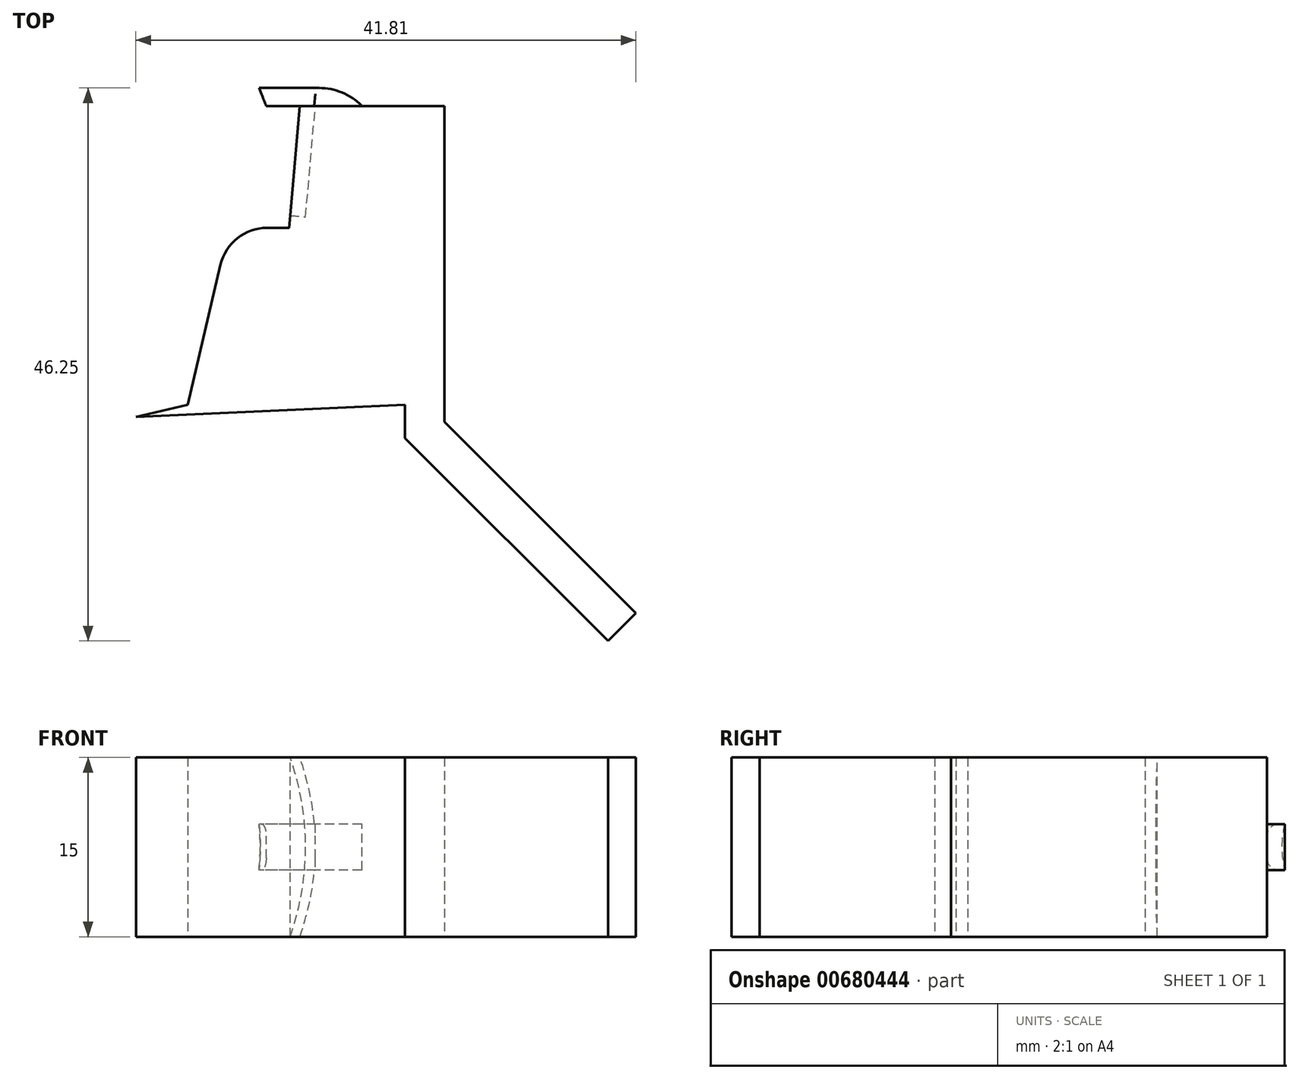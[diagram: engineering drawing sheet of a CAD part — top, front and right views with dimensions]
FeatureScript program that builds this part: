
annotation { "Feature Type Name" : "Feature", "Feature Type Description" : "" }
export const myFeature = defineFeature(function(context is Context, id is Id, definition is map)
    precondition{}
    {
        {
            var Q0;
            Q0=qCreatedBy(makeId("Top.planeOp"),FACE);
            var sketch = newSketch(context, id + "F0", { "sketchPlane" : qUnion([Q0])});
            skLineSegment(sketch, "E0", {"start": v(21, -3.41) * mm, "end": v(21, 23) * mm});
            skLineSegment(sketch, "E1", {"start": v(21, 23) * mm, "end": v(8.9, 23) * mm});
            skLineSegment(sketch, "E2", {"start": v(6.17, 12.8) * mm, "end": v(8, 12.8) * mm});
            skLineSegment(sketch, "E3", {"start": v(-0.47, -2) * mm, "end": v(2.28, 9.71) * mm});
            skLineSegment(sketch, "E4", {"start": v(8.9, 23) * mm, "end": v(8, 12.8) * mm});
            skPoint(sketch, "E5.visualSharp", {"position": v(3, 12.8) * mm});
            skArc(sketch, "E5.filletArc", {"start": v(6.17, 12.8) * mm, "mid": v(3.69, 11.93) * mm, "end": v(2.28, 9.71) * mm});
            skPoint(sketch, "E6.visualSharp", {"position": v(8, 12.8) * mm});
            skArc(sketch, "E6.filletArc", {"start": v(8, 12.8) * mm, "mid": v(8, 12.8) * mm, "end": v(8, 12.8) * mm});
            skLineSegment(sketch, "E7.trimOffspring", {"start": v(21, -3.41) * mm, "end": v(37, -19.42) * mm});
            skLineSegment(sketch, "E8.0", {"start": v(17.7, -4.78) * mm, "end": v(34.68, -21.75) * mm});
            skLineSegment(sketch, "E9", {"start": v(17.7, -4.78) * mm, "end": v(17.7, -2) * mm});
            skLineSegment(sketch, "E10", {"start": v(34.68, -21.75) * mm, "end": v(37, -19.42) * mm});
            skLineSegment(sketch, "E11.0", {"start": v(-4.8, -3) * mm, "end": v(17.7, -2) * mm});
            skLineSegment(sketch, "E12", {"start": v(-4.8, -3) * mm, "end": v(-0.47, -2) * mm});
            skSolve(sketch);
        }
        {
            var Q0;
            Q0 = qSketchRegion(id + "F0", true);
            extrude(context, id + "F1", {"entities" : qUnion([Q0]), "depth" : 15 * mm, "offsetDistance" : 25 * mm});
        }
        {
            var Q0;
            Q0=makeQuery(id+"F1.opExtrude","CAP_VERTEX",VERTEX,{"disambiguationData":[OSD([sQuery(id+"F0.wireOp",EDGE,"E1"),sQuery(id+"F0.wireOp",EDGE,"E4")])],"isStart":true});
            var Q1;
            Q1=makeQuery(id+"F1.opExtrude","CAP_EDGE",EDGE,{"disambiguationData":[OSD([sQuery(id+"F0.wireOp",EDGE,"E4")])],"isStart":false});
            cPlane(context, id + "F2", {"entities" : qUnion([Q0, Q1]), "cplaneType" : CPlaneType.LINE_POINT, "offset" : 25 * mm, "width" : 150 * mm, "height" : 150 * mm});
        }
        {
            var Q0;
            Q0=qCreatedBy(id+"F2.planeOp",FACE);
            var sketch = newSketch(context, id + "F3", { "sketchPlane" : qUnion([Q0])});
            skLineSegment(sketch, "E13", {"start": v(6.84, 0) * mm, "end": v(6.84, 15) * mm});
            skArc(sketch, "E14", {"start": v(6.84, 0) * mm, "mid": v(8.14, 7.5) * mm, "end": v(6.84, 15) * mm});
            skPoint(sketch, "E15.start.orphan", {"position": v(6.84, 7.5) * mm});
            skSolve(sketch);
        }
        {
            var Q0;
            Q0 = qSketchRegion(id + "F3", true);
            extrude(context, id + "F4", {"entities" : qUnion([Q0]), "operationType" : NewBodyOperationType.REMOVE, "depth" : 9.2 * mm, "offsetDistance" : 25 * mm, "hasSecondDirection" : true, "secondDirectionOppositeDirection" : true, "secondDirectionDepth" : 1 * mm});
        }
        {
            var Q0;
            Q0=makeQuery(id+"F1.opExtrude","SWEPT_FACE",FACE,{"disambiguationData":[OSD([sQuery(id+"F0.wireOp",EDGE,"E1")])]});
            cPlane(context, id + "F5", {"entities" : qUnion([Q0]), "cplaneType" : CPlaneType.OFFSET, "offset" : 0 * mm, "width" : 150 * mm, "height" : 150 * mm});
        }
        {
            var Q0;
            Q0=qCreatedBy(id+"F5.planeOp",FACE);
            var sketch = newSketch(context, id + "F6", { "sketchPlane" : qUnion([Q0])});
            skLineSegment(sketch, "E16.0", {"start": v(-14.1, 5.58) * mm, "end": v(-5.5, 5.58) * mm});
            skLineSegment(sketch, "E17.0", {"start": v(-14.1, 9.42) * mm, "end": v(-5.5, 9.42) * mm});
            skArc(sketch, "E18", {"start": v(-7, 9.42) * mm, "mid": v(-7.1, 7.5) * mm, "end": v(-7, 5.58) * mm});
            skLineSegment(sketch, "E19", {"start": v(-14.1, 7.5) * mm, "end": v(-14.1, 5.58) * mm});
            skLineSegment(sketch, "E20", {"start": v(-14.1, 7.5) * mm, "end": v(-14.1, 9.42) * mm});
            skPoint(sketch, "E21.orphan", {"position": v(-11.1, 5.58) * mm});
            skPoint(sketch, "E22.orphan", {"position": v(-11.1, 9.42) * mm});
            skArc(sketch, "E23.0", {"start": v(-5.5, 9.42) * mm, "mid": v(-5.6, 7.5) * mm, "end": v(-5.5, 5.58) * mm});
            skSolve(sketch);
        }
        {
            var Q0;
            {var subQ2=sQuery(id+"F6.wireOp",EDGE,"E18");Q0=makeQuery(id+"F6.imprint","IMPRINT",FACE,{"disambiguationData":[TD([[makeQuery(id+"F6.imprint","IMPRINT",EDGE,{"derivedFrom":subQ2}),1.0]])]});}
            var Q1;
            {var subQ0=sQuery(id+"F6.wireOp",EDGE,"E18");Q1=makeQuery(id+"F6.imprint","IMPRINT",FACE,{"disambiguationData":[TD([[makeQuery(id+"F6.imprint","IMPRINT",EDGE,{"derivedFrom":subQ0}),-1.0]])]});}
            extrude(context, id + "F7", {"entities" : qUnion([Q0, Q1]), "operationType" : NewBodyOperationType.ADD, "depth" : 1.5 * mm, "offsetDistance" : 25 * mm});
        }
        {
            var Q0;
            Q0=makeQuery(id+"F7.opExtrude","CAP_EDGE",EDGE,{"disambiguationData":[OSD([sQuery(id+"F6.wireOp",EDGE,"E19"),sQuery(id+"F6.wireOp",EDGE,"E20")])],"isStart":false});
            chamfer(context, id + "F8", {"entities" : qUnion([Q0]), "width" : 1.5 * mm, "tangentPropagation" : true});
        }
        {
            var Q0;
            {var subQ0=sQuery(id+"F6.wireOp",EDGE,"E20");var subQ1=sQuery(id+"F6.wireOp",EDGE,"E19");Q0=makeQuery(id+"F8.opChamfer","BLEND_EDGE",EDGE,{"blendedFrom":[makeQuery(id+"F7.opExtrude","CAP_EDGE",EDGE,{"disambiguationData":[OSD([subQ1,subQ0])],"isStart":false}),makeQuery(id+"F7.opExtrude","CAP_FACE",FACE,{"disambiguationData":[OSD([sQuery(id+"F6.wireOp",EDGE,"E16.0"),sQuery(id+"F6.wireOp",EDGE,"E17.0"),sQuery(id+"F6.wireOp",EDGE,"E18"),subQ1,subQ0])],"isStart":false})],"blendedInto":[makeQuery(id+"F7.opExtrude","CAP_FACE",FACE,{"disambiguationData":[OSD([sQuery(id+"F6.wireOp",EDGE,"E16.0"),sQuery(id+"F6.wireOp",EDGE,"E17.0"),sQuery(id+"F6.wireOp",EDGE,"E18"),subQ1,subQ0])],"isStart":false})]});}
            fillet(context, id + "F9", {"entities" : qUnion([Q0]), "radius" : 5 * mm, "tangentPropagation" : true, "allowEdgeOverflow" : false});
        }
        {
            var Q0;
            {var subQ0=sQuery(id+"F6.wireOp",EDGE,"E17.0");Q0=makeQuery(id+"Fht0wsbCu2fpYdC_1.boolean.opBoolean","MERGE",FACE,{"derivedFrom":[makeQuery(id+"F7.opExtrude","SWEPT_FACE",FACE,{"disambiguationData":[OSD([subQ0])]}),makeQuery(id+"Fht0wsbCu2fpYdC_1.opExtrude","SWEPT_FACE",FACE,{"disambiguationData":[OSD([subQ0])]})]});}
            var sketch = newSketch(context, id + "F10", { "sketchPlane" : qUnion([Q0])});
            skLineSegment(sketch, "E24", {"start": v(6.5, 22) * mm, "end": v(5.5, 24.5) * mm});
            skLineSegment(sketch, "E25", {"start": v(5.5, 24.5) * mm, "end": v(5.5, 22) * mm});
            skLineSegment(sketch, "E26", {"start": v(5.5, 22) * mm, "end": v(6.5, 22) * mm});
            skSolve(sketch);
        }
        {
            var Q0;
            Q0=makeQuery(id+"F10.imprint","IMPRINT",FACE,{"disambiguationData":[TD([[makeQuery(id+"F10.imprint","IMPRINT",EDGE,{"derivedFrom":sQuery(id+"F10.wireOp",EDGE,"E24")}),1.0]])]});
            extrude(context, id + "F11", {"entities" : qUnion([Q0]), "operationType" : NewBodyOperationType.REMOVE, "oppositeDirection" : true, "depth" : 4 * mm, "offsetDistance" : 25 * mm});
        }
        {
            var Q0;
            {var subQ0=sQuery(id+"F6.wireOp",EDGE,"E17.0");Q0=makeQuery(id+"F7.boolean.opBoolean","SPLIT",EDGE,{"disambiguationData":[topologyDisambiguationEdgeConnected([makeQuery(id+"F1.opExtrude","SWEPT_FACE",FACE,{"disambiguationData":[OSD([sQuery(id+"F0.wireOp",EDGE,"E1")])]})])],"derivedFrom":makeQuery(id+"F7.opExtrude","CAP_EDGE",EDGE,{"disambiguationData":[OSD([subQ0])],"isStart":true})});}
            var Q1;
            {var subQ0=sQuery(id+"F6.wireOp",EDGE,"E20");var subQ1=sQuery(id+"F6.wireOp",EDGE,"E19");Q1=makeQuery(id+"F9.opFillet","BLEND_EDGE",EDGE,{"blendedFrom":[makeQuery(id+"F8.opChamfer","BLEND_EDGE",EDGE,{"blendedFrom":[makeQuery(id+"F7.opExtrude","CAP_EDGE",EDGE,{"disambiguationData":[OSD([subQ1,subQ0])],"isStart":false}),makeQuery(id+"F7.opExtrude","CAP_FACE",FACE,{"disambiguationData":[OSD([sQuery(id+"F6.wireOp",EDGE,"E16.0"),sQuery(id+"F6.wireOp",EDGE,"E17.0"),sQuery(id+"F6.wireOp",EDGE,"E18"),subQ1,subQ0])],"isStart":false})],"blendedInto":[makeQuery(id+"F7.opExtrude","CAP_FACE",FACE,{"disambiguationData":[OSD([sQuery(id+"F6.wireOp",EDGE,"E16.0"),sQuery(id+"F6.wireOp",EDGE,"E17.0"),sQuery(id+"F6.wireOp",EDGE,"E18"),subQ1,subQ0])],"isStart":false})]}),makeQuery(id+"F8.opChamfer","BLEND_FACE",FACE,{"disambiguationData":[OSD([subQ1,subQ0])]})],"blendedInto":[makeQuery(id+"F8.opChamfer","BLEND_FACE",FACE,{"disambiguationData":[OSD([subQ1,subQ0])]})]});}
            var Q2;
            {var subQ0=sQuery(id+"F6.wireOp",EDGE,"E16.0");Q2=makeQuery(id+"F7.boolean.opBoolean","SPLIT",EDGE,{"disambiguationData":[topologyDisambiguationEdgeConnected([makeQuery(id+"F1.opExtrude","SWEPT_FACE",FACE,{"disambiguationData":[OSD([sQuery(id+"F0.wireOp",EDGE,"E1")])]})])],"derivedFrom":makeQuery(id+"F7.opExtrude","CAP_EDGE",EDGE,{"disambiguationData":[OSD([subQ0])],"isStart":true})});}
            fillet(context, id + "F12", {"entities" : qUnion([Q0, Q1, Q2]), "radius" : 1 * mm, "tangentPropagation" : true, "allowEdgeOverflow" : false});
        }
    });
